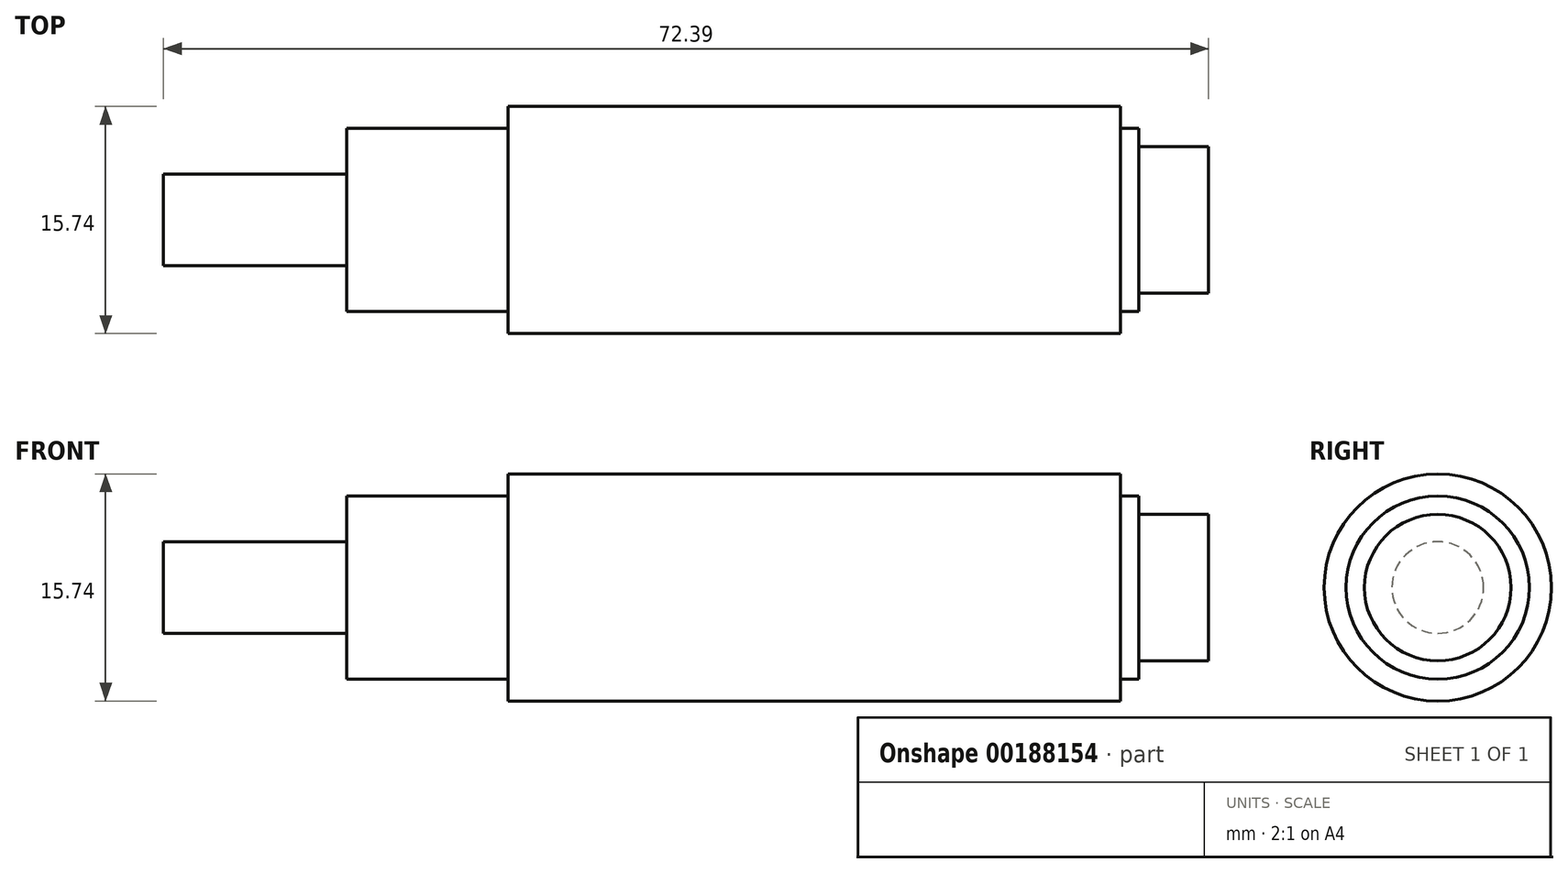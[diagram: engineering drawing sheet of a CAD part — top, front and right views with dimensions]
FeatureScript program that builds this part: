
annotation { "Feature Type Name" : "Feature", "Feature Type Description" : "" }
export const myFeature = defineFeature(function(context is Context, id is Id, definition is map)
    precondition{}
    {
        {
            var Q0;
            Q0=qCreatedBy(makeId("Front.planeOp"),FACE);
            var sketch = newSketch(context, id + "F0", { "sketchPlane" : qUnion([Q0])});
            skLineSegment(sketch, "E0", {"start": v(-12.7, 0) * mm, "end": v(-12.7, 3.17) * mm});
            skLineSegment(sketch, "E1", {"start": v(-12.7, 3.17) * mm, "end": v(0, 3.17) * mm});
            skLineSegment(sketch, "E2", {"start": v(0, 3.17) * mm, "end": v(0, 6.35) * mm});
            skLineSegment(sketch, "E3", {"start": v(0, 6.35) * mm, "end": v(11.18, 6.35) * mm});
            skLineSegment(sketch, "E4", {"start": v(11.18, 7.87) * mm, "end": v(11.18, 6.35) * mm});
            skLineSegment(sketch, "E5", {"start": v(11.18, 7.87) * mm, "end": v(53.6, 7.87) * mm});
            skLineSegment(sketch, "E6", {"start": v(53.6, 6.35) * mm, "end": v(53.6, 7.87) * mm});
            skLineSegment(sketch, "E7", {"start": v(53.6, 6.35) * mm, "end": v(54.86, 6.35) * mm});
            skLineSegment(sketch, "E8", {"start": v(54.86, 6.35) * mm, "end": v(54.86, 5.08) * mm});
            skLineSegment(sketch, "E9", {"start": v(54.86, 5.08) * mm, "end": v(59.7, 5.08) * mm});
            skLineSegment(sketch, "E10", {"start": v(59.7, 5.08) * mm, "end": v(59.7, 0) * mm});
            skLineSegment(sketch, "E11", {"start": v(-12.7, 0) * mm, "end": v(59.7, 0) * mm});
            skLineSegment(sketch, "E12", {"start": v(0, 3.17) * mm, "end": v(0, 0) * mm, "construction": true});
            skLineSegment(sketch, "E13", {"start": v(-33.18, 0) * mm, "end": v(86.2, 0) * mm, "construction": true});
            skSolve(sketch);
        }
        {
            var Q0;
            Q0 = qSketchRegion(id + "F0", true);
            var Q1;
            Q1=sQuery(id+"F0.wireOp",EDGE,"E13");
            revolve(context, id + "F1", {"entities" : qUnion([Q0]), "axis" : qUnion([Q1]), "revolveType" : RevolveType.FULL});
        }
    });
